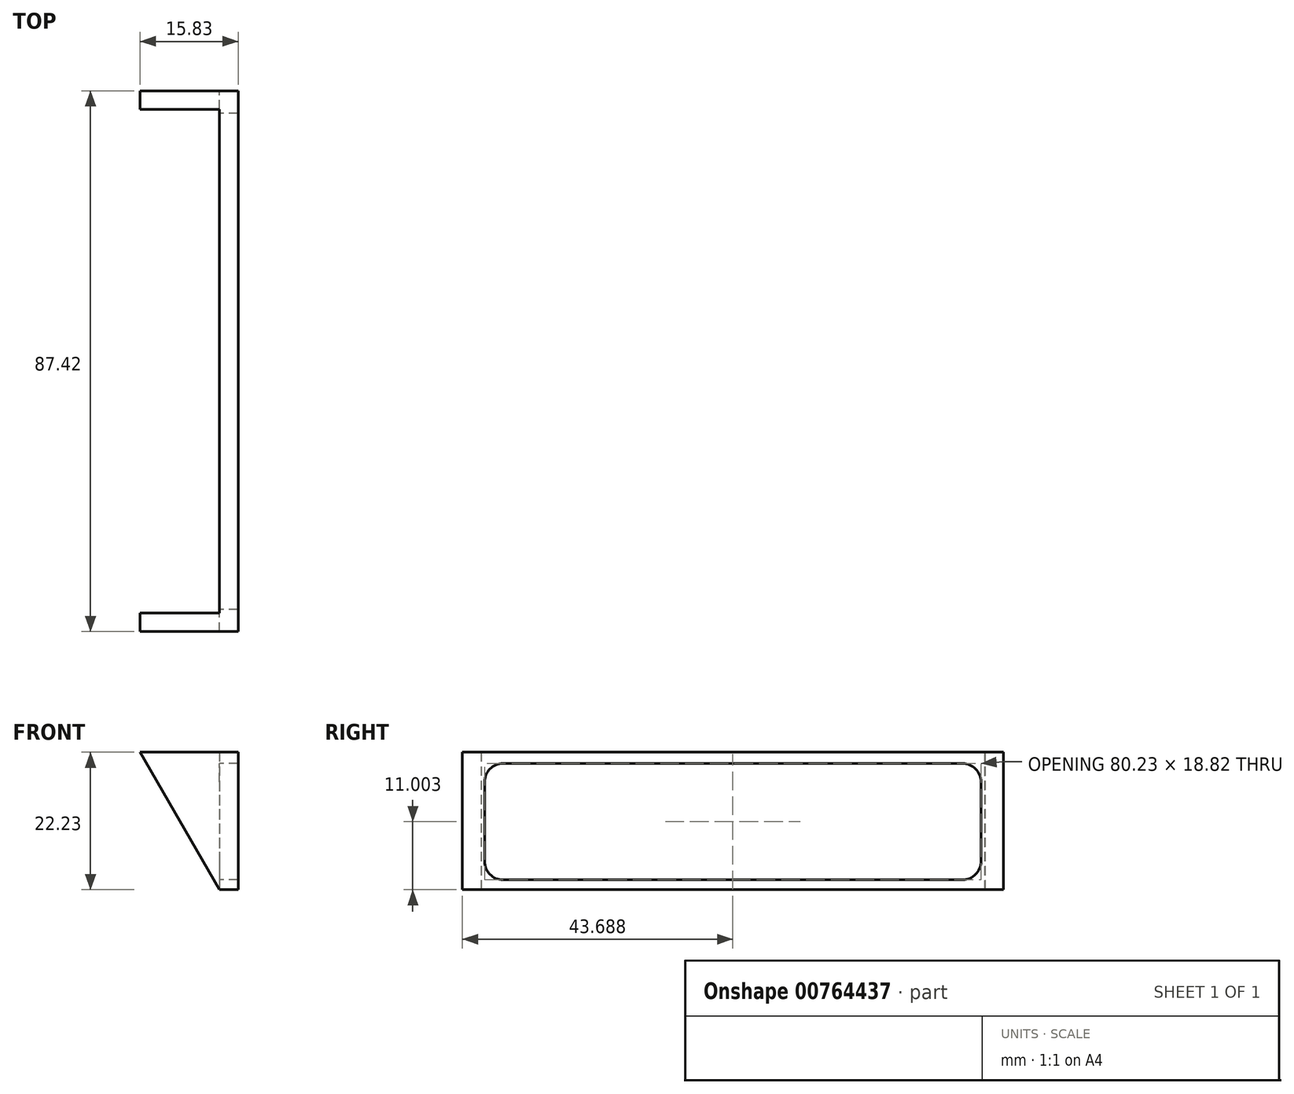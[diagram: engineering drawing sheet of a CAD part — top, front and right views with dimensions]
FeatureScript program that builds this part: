
annotation { "Feature Type Name" : "Feature", "Feature Type Description" : "" }
export const myFeature = defineFeature(function(context is Context, id is Id, definition is map)
    precondition{}
    {
        {
            var Q0;
            Q0=qCreatedBy(makeId("Right.planeOp"),FACE);
            var sketch = newSketch(context, id + "F0", { "sketchPlane" : qUnion([Q0])});
            skLineSegment(sketch, "E0.left", {"start": v(-41.6, -6.42) * mm, "end": v(-41.6, 6.2) * mm});
            skPoint(sketch, "E1.visualSharp", {"position": v(-41.6, 10.2) * mm});
            skPoint(sketch, "E2.visualSharp", {"position": v(-41.6, -10.42) * mm});
            skPoint(sketch, "E3.visualSharp", {"position": v(41.56, 10.2) * mm});
            skPoint(sketch, "E4.visualSharp", {"position": v(41.56, -10.42) * mm});
            skPoint(sketch, "E5.visualSharp", {"position": v(-38.3, -8.6) * mm});
            skPoint(sketch, "E6.visualSharp", {"position": v(38.25, -8.6) * mm});
            skLineSegment(sketch, "E7.bottom", {"start": v(-37.14, 9.3) * mm, "end": v(37.1, 9.3) * mm});
            skLineSegment(sketch, "E7.top", {"start": v(-37.14, -9.52) * mm, "end": v(37.1, -9.52) * mm});
            skLineSegment(sketch, "E7.left", {"start": v(-40.14, 6.3) * mm, "end": v(-40.14, -6.52) * mm});
            skLineSegment(sketch, "E7.right", {"start": v(40.1, 6.3) * mm, "end": v(40.1, -6.52) * mm});
            skArc(sketch, "E8.filletArc", {"start": v(-37.14, 9.3) * mm, "mid": v(-39.26, 8.42) * mm, "end": v(-40.14, 6.3) * mm});
            skPoint(sketch, "E9.visualSharp", {"position": v(-40.14, -9.52) * mm});
            skArc(sketch, "E9.filletArc", {"start": v(-40.14, -6.52) * mm, "mid": v(-39.26, -8.64) * mm, "end": v(-37.14, -9.52) * mm});
            skArc(sketch, "E10.filletArc", {"start": v(37.1, -9.52) * mm, "mid": v(39.21, -8.64) * mm, "end": v(40.1, -6.52) * mm});
            skArc(sketch, "E11.filletArc", {"start": v(40.1, 6.3) * mm, "mid": v(39.21, 8.42) * mm, "end": v(37.1, 9.3) * mm});
            skLineSegment(sketch, "E12.bottom", {"start": v(-43.7, 11.11) * mm, "end": v(43.7, 11.11) * mm});
            skLineSegment(sketch, "E12.top", {"start": v(-43.7, -11.11) * mm, "end": v(43.7, -11.11) * mm});
            skLineSegment(sketch, "E12.left", {"start": v(-43.7, 11.11) * mm, "end": v(-43.7, -11.11) * mm});
            skLineSegment(sketch, "E12.right", {"start": v(43.7, 11.11) * mm, "end": v(43.7, -11.11) * mm});
            skPoint(sketch, "E12.middle", {"position": v(0, 0) * mm});
            skLineSegment(sketch, "E13.bottom", {"start": v(-43.7, 11.11) * mm, "end": v(-41.6, 11.11) * mm});
            skLineSegment(sketch, "E13.top", {"start": v(-43.7, -11.11) * mm, "end": v(-41.6, -11.11) * mm});
            skLineSegment(sketch, "E13.right", {"start": v(-41.6, 11.11) * mm, "end": v(-41.6, -11.11) * mm});
            skLineSegment(sketch, "E14.bottom", {"start": v(43.7, 11.11) * mm, "end": v(41.56, 11.11) * mm});
            skLineSegment(sketch, "E14.top", {"start": v(43.7, -11.11) * mm, "end": v(41.56, -11.11) * mm});
            skLineSegment(sketch, "E14.right", {"start": v(41.56, 11.11) * mm, "end": v(41.56, -11.11) * mm});
            skSolve(sketch);
        }
        {
            var Q0;
            {var subQ0=sQuery(id+"F0.wireOp",EDGE,"E12.right");var subQ11=sQuery(id+"F0.wireOp",EDGE,"E0.left");var subQ12=makeQuery(id+"F0.imprint","IMPRINT",EDGE,{"derivedFrom":subQ11});Q0=qUnion([makeQuery(id+"F0.imprint","IMPRINT",FACE,{"disambiguationData":[TD([[subQ12,-1.0]])]}),makeQuery(id+"F0.imprint","IMPRINT",FACE,{"disambiguationData":[TD([[subQ12,1.0]])]}),makeQuery(id+"F0.imprint","IMPRINT",FACE,{"disambiguationData":[TD([[makeQuery(id+"F0.imprint","IMPRINT",EDGE,{"derivedFrom":subQ0}),-1.0]])]})]);}
            extrude(context, id + "F1", {"entities" : qUnion([Q0]), "depth" : 3 * mm, "offsetDistance" : 25 * mm});
        }
        {
            var Q0;
            Q0=makeQuery(id+"F1.opExtrude","SWEPT_FACE",FACE,{"disambiguationData":[OSD([sQuery(id+"F0.wireOp",EDGE,"E12.left")])]});
            var sketch = newSketch(context, id + "F2", { "sketchPlane" : qUnion([Q0])});
            skLineSegment(sketch, "E15", {"start": v(0, 11.11) * mm, "end": v(-12.83, 11.11) * mm});
            skLineSegment(sketch, "E16", {"start": v(-12.83, 11.11) * mm, "end": v(0, -11.11) * mm});
            skSolve(sketch);
        }
        {
            var Q0;
            Q0 = qSketchRegion(id + "F2", true);
            var Q1;
            Q1=makeQuery(id+"F2.imprint","IMPRINT",FACE,{"disambiguationData":[TD([[makeQuery(id+"F2.imprint","IMPRINT",EDGE,{"derivedFrom":sQuery(id+"F2.wireOp",EDGE,"E15")}),1.0]])]});
            extrude(context, id + "F3", {"entities" : qUnion([Q0, Q1]), "operationType" : NewBodyOperationType.ADD, "oppositeDirection" : true, "depth" : 3 * mm, "offsetDistance" : 25 * mm});
        }
        {
            var Q0;
            Q0=makeQuery(id+"F1.opExtrude","SWEPT_FACE",FACE,{"disambiguationData":[OSD([sQuery(id+"F0.wireOp",EDGE,"E12.right")])]});
            var sketch = newSketch(context, id + "F4", { "sketchPlane" : qUnion([Q0])});
            skLineSegment(sketch, "E17", {"start": v(0, 11.11) * mm, "end": v(0, -11.11) * mm});
            skLineSegment(sketch, "E18", {"start": v(0, -11.11) * mm, "end": v(12.82, 11.12) * mm});
            skLineSegment(sketch, "E19", {"start": v(12.82, 11.12) * mm, "end": v(0, 11.11) * mm});
            skSolve(sketch);
        }
        {
            var Q0;
            Q0=makeQuery(id+"F4.imprint","IMPRINT",FACE,{"disambiguationData":[TD([[makeQuery(id+"F4.imprint","IMPRINT",EDGE,{"derivedFrom":sQuery(id+"F4.wireOp",EDGE,"E17")}),1.0]])]});
            extrude(context, id + "F5", {"entities" : qUnion([Q0]), "operationType" : NewBodyOperationType.ADD, "oppositeDirection" : true, "depth" : 3 * mm, "offsetDistance" : 25 * mm});
        }
    });
